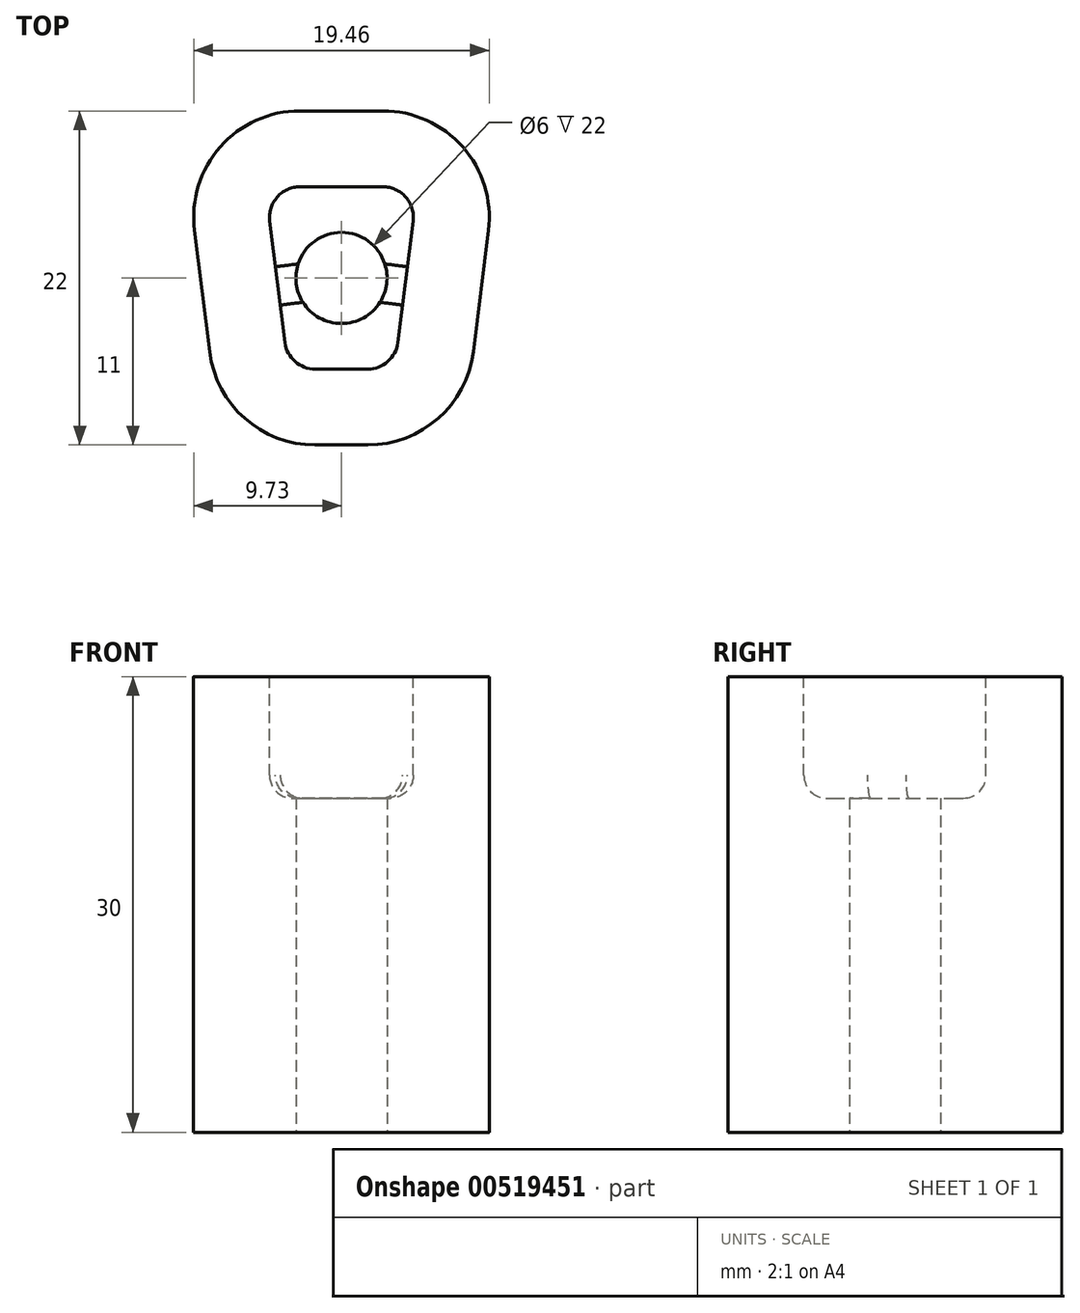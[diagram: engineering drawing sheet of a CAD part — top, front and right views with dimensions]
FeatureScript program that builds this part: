
annotation { "Feature Type Name" : "Feature", "Feature Type Description" : "" }
export const myFeature = defineFeature(function(context is Context, id is Id, definition is map)
    precondition{}
    {
        {
            var Q0;
            Q0=qCreatedBy(makeId("Top.planeOp"),FACE);
            var sketch = newSketch(context, id + "F0", { "sketchPlane" : qUnion([Q0])});
            skLineSegment(sketch, "E0", {"start": v(0, 0) * mm, "end": v(1.73, 0) * mm});
            skLineSegment(sketch, "E1", {"start": v(0, 0) * mm, "end": v(0, 12) * mm});
            skLineSegment(sketch, "E2", {"start": v(0, 12) * mm, "end": v(2.73, 12) * mm});
            skLineSegment(sketch, "E3", {"start": v(3.72, 1.75) * mm, "end": v(4.72, 9.75) * mm});
            skPoint(sketch, "E4.visualSharp", {"position": v(5, 12) * mm});
            skArc(sketch, "E4.filletArc", {"start": v(4.72, 9.75) * mm, "mid": v(4.23, 11.32) * mm, "end": v(2.73, 12) * mm});
            skPoint(sketch, "E5.visualSharp", {"position": v(3.5, 0) * mm});
            skArc(sketch, "E5.filletArc", {"start": v(1.73, 0) * mm, "mid": v(3.06, 0.5) * mm, "end": v(3.72, 1.75) * mm});
            skLineSegment(sketch, "E6.MirrorCS", {"start": v(0, 12) * mm, "end": v(-2.73, 12) * mm});
            skArc(sketch, "E7.MirrorCS", {"start": v(-4.72, 9.75) * mm, "mid": v(-4.23, 11.32) * mm, "end": v(-2.73, 12) * mm});
            skLineSegment(sketch, "E8.MirrorCS", {"start": v(-3.72, 1.75) * mm, "end": v(-4.72, 9.75) * mm});
            skArc(sketch, "E9.MirrorCS", {"start": v(-1.73, 0) * mm, "mid": v(-3.06, 0.5) * mm, "end": v(-3.72, 1.75) * mm});
            skLineSegment(sketch, "E10.MirrorCS", {"start": v(0, 0) * mm, "end": v(-1.73, 0) * mm});
            skLineSegment(sketch, "E11.0", {"start": v(0, 17) * mm, "end": v(2.73, 17) * mm});
            skArc(sketch, "E12.0", {"start": v(9.68, 9.13) * mm, "mid": v(7.98, 14.63) * mm, "end": v(2.73, 17) * mm});
            skLineSegment(sketch, "E13.0", {"start": v(8.68, 1.13) * mm, "end": v(9.68, 9.13) * mm});
            skArc(sketch, "E14.0", {"start": v(1.73, -5) * mm, "mid": v(6.37, -3.25) * mm, "end": v(8.68, 1.13) * mm});
            skLineSegment(sketch, "E15.0", {"start": v(0, -5) * mm, "end": v(1.73, -5) * mm});
            skLineSegment(sketch, "E16.0", {"start": v(0, -5) * mm, "end": v(-1.73, -5) * mm});
            skArc(sketch, "E17.0", {"start": v(-1.73, -5) * mm, "mid": v(-6.37, -3.25) * mm, "end": v(-8.68, 1.13) * mm});
            skLineSegment(sketch, "E18.0", {"start": v(-8.68, 1.13) * mm, "end": v(-9.68, 9.13) * mm});
            skArc(sketch, "E19.0", {"start": v(-9.68, 9.13) * mm, "mid": v(-7.98, 14.63) * mm, "end": v(-2.73, 17) * mm});
            skLineSegment(sketch, "E20.0", {"start": v(0, 17) * mm, "end": v(-2.73, 17) * mm});
            skCircle(sketch, "E21", {"center": v(0, 6) * mm, "radius": 3 * mm});
            skSolve(sketch);
        }
        {
            var Q0;
            Q0=qCreatedBy(makeId("Top.planeOp"),FACE);
            cPlane(context, id + "F1", {"entities" : qUnion([Q0]), "cplaneType" : CPlaneType.OFFSET, "offset" : 30 * mm, "width" : 150 * mm, "height" : 150 * mm});
        }
        {
            var Q0;
            Q0=qCreatedBy(id+"F1.planeOp",FACE);
            var sketch = newSketch(context, id + "F2", { "sketchPlane" : qUnion([Q0])});
            skLineSegment(sketch, "E22.0.0", {"start": v(-1.73, 0) * mm, "end": v(0, 0) * mm});
            skLineSegment(sketch, "E22.0.1", {"start": v(0, 0) * mm, "end": v(0, 3) * mm});
            skArc(sketch, "E22.0.2", {"start": v(0, 3) * mm, "mid": v(-3, 6) * mm, "end": v(0, 9) * mm});
            skLineSegment(sketch, "E22.0.3", {"start": v(0, 9) * mm, "end": v(0, 12) * mm});
            skLineSegment(sketch, "E22.0.4", {"start": v(0, 12) * mm, "end": v(-2.73, 12) * mm});
            skArc(sketch, "E22.0.5", {"start": v(-2.73, 12) * mm, "mid": v(-4.23, 11.32) * mm, "end": v(-4.72, 9.75) * mm});
            skLineSegment(sketch, "E22.0.6", {"start": v(-4.72, 9.75) * mm, "end": v(-3.72, 1.75) * mm});
            skArc(sketch, "E22.0.7", {"start": v(-3.72, 1.75) * mm, "mid": v(-3.06, 0.5) * mm, "end": v(-1.73, 0) * mm});
            skLineSegment(sketch, "E22.1.0", {"start": v(3.72, 1.75) * mm, "end": v(4.72, 9.75) * mm});
            skArc(sketch, "E22.1.1", {"start": v(4.72, 9.75) * mm, "mid": v(4.23, 11.32) * mm, "end": v(2.73, 12) * mm});
            skLineSegment(sketch, "E22.1.2", {"start": v(2.73, 12) * mm, "end": v(0, 12) * mm});
            skLineSegment(sketch, "E22.1.3", {"start": v(0, 12) * mm, "end": v(0, 9) * mm});
            skArc(sketch, "E22.1.4", {"start": v(0, 9) * mm, "mid": v(3, 6) * mm, "end": v(0, 3) * mm});
            skLineSegment(sketch, "E22.1.5", {"start": v(0, 3) * mm, "end": v(0, 0) * mm});
            skLineSegment(sketch, "E22.1.6", {"start": v(0, 0) * mm, "end": v(1.73, 0) * mm});
            skArc(sketch, "E22.1.7", {"start": v(1.73, 0) * mm, "mid": v(3.06, 0.5) * mm, "end": v(3.72, 1.75) * mm});
            skSolve(sketch);
        }
        {
            var Q0;
            Q0=makeQuery(id+"F0.imprint","IMPRINT",FACE,{"disambiguationData":[TD([[makeQuery(id+"F0.imprint","IMPRINT",EDGE,{"derivedFrom":sQuery(id+"F0.wireOp",EDGE,"E0")}),-1.0]])]});
            var Q1;
            {var subQ0=sQuery(id+"F0.wireOp",EDGE,"E6.MirrorCS");Q1=makeQuery(id+"F0.imprint","IMPRINT",FACE,{"disambiguationData":[TD([[makeQuery(id+"F0.imprint","IMPRINT",EDGE,{"derivedFrom":subQ0}),1.0]])]});}
            var Q2;
            {var subQ4=sQuery(id+"F0.wireOp",EDGE,"E0");Q2=makeQuery(id+"F0.imprint","IMPRINT",FACE,{"disambiguationData":[TD([[makeQuery(id+"F0.imprint","IMPRINT",EDGE,{"derivedFrom":subQ4}),1.0]])]});}
            extrude(context, id + "F3", {"entities" : qUnion([Q0, Q1, Q2]), "depth" : 30 * mm, "offsetDistance" : 25 * mm});
        }
        {
            var Q0;
            Q0=makeQuery(id+"F2.imprint","IMPRINT",FACE,{"disambiguationData":[TD([[makeQuery(id+"F2.imprint","IMPRINT",EDGE,{"derivedFrom":sQuery(id+"F2.wireOp",EDGE,"E22.0.0")}),1.0]])]});
            var Q1;
            Q1=makeQuery(id+"F2.imprint","IMPRINT",FACE,{"disambiguationData":[TD([[makeQuery(id+"F2.imprint","IMPRINT",EDGE,{"derivedFrom":sQuery(id+"F2.wireOp",EDGE,"E22.1.0")}),1.0]])]});
            extrude(context, id + "F4", {"entities" : qUnion([Q0, Q1]), "operationType" : NewBodyOperationType.REMOVE, "oppositeDirection" : true, "depth" : 8 * mm, "offsetDistance" : 25 * mm});
        }
        {
            var Q0;
            Q0=makeQuery(id+"F4.boolean.opBoolean","COPY",EDGE,{"derivedFrom":makeQuery(id+"F4.opExtrude","CAP_EDGE",EDGE,{"disambiguationData":[OSD([sQuery(id+"F2.wireOp",EDGE,"E22.0.5")])],"isStart":false})});
            var Q1;
            Q1=makeQuery(id+"F4.boolean.opBoolean","COPY",EDGE,{"derivedFrom":makeQuery(id+"F4.opExtrude","CAP_EDGE",EDGE,{"disambiguationData":[OSD([sQuery(id+"F2.wireOp",EDGE,"E22.0.6")])],"isStart":false})});
            fillet(context, id + "F5", {"entities" : qUnion([Q0, Q1]), "radius" : 1.5 * mm, "tangentPropagation" : true, "allowEdgeOverflow" : false});
        }
    });
